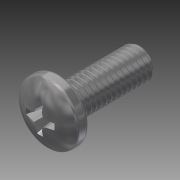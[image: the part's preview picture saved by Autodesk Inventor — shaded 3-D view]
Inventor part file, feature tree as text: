
AUTODESK INVENTOR PART (.ipt)
format: ipt  version: 2014 SP1 (Build 180222100, 222)  size: 683,008 bytes
history: native  units: in
note: dims shown in document units (in); Inventor stores cm internally (conversion verified against a paired STEP export)
features: fillet x1, other x1, imported_body x1
ambient origin geometry x8: Origin, YZ Plane, XZ Plane, XY Plane, X Axis, Y Axis, Z Axis, Center Point
bodies: Body1 (feature_tree)
feature tree (3):
  fillet  "Fillet1"  [1 undecoded]
  other  "91735A8291"
  imported_body  "Base1"
note: 1 required parameter value undecoded (feature->parameter linkage not recoverable at this tier; creation-order binding heuristic only, values carry confidence <= 0.55)
